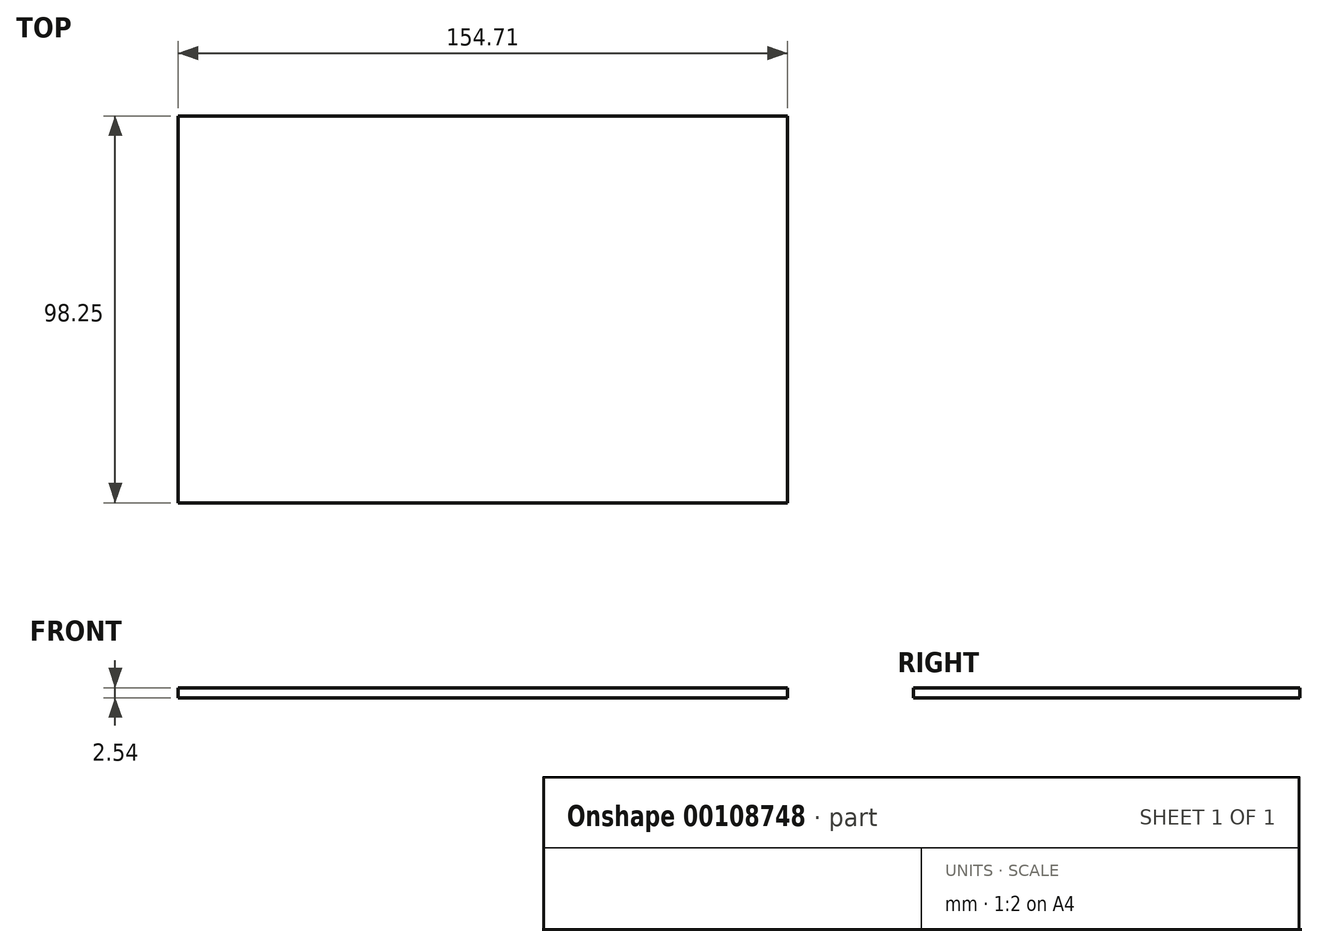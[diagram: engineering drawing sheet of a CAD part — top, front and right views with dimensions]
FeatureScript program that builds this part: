
annotation { "Feature Type Name" : "Feature", "Feature Type Description" : "" }
export const myFeature = defineFeature(function(context is Context, id is Id, definition is map)
    precondition{}
    {
        {
            var Q0;
            Q0=qCreatedBy(makeId("Top.planeOp"),FACE);
            var sketch = newSketch(context, id + "F0", { "sketchPlane" : qUnion([Q0])});
            skLineSegment(sketch, "E0.bottom", {"start": v(-39.4, 27.04) * mm, "end": v(115.3, 27.04) * mm});
            skLineSegment(sketch, "E0.top", {"start": v(-39.4, -71.21) * mm, "end": v(115.3, -71.21) * mm});
            skLineSegment(sketch, "E0.left", {"start": v(-39.4, 27.04) * mm, "end": v(-39.4, -71.21) * mm});
            skLineSegment(sketch, "E0.right", {"start": v(115.3, 27.04) * mm, "end": v(115.3, -71.21) * mm});
            skSolve(sketch);
        }
        {
            var Q0;
            Q0 = qSketchRegion(id + "F0", true);
            extrude(context, id + "F1", {"entities" : qUnion([Q0]), "depth" : 2.54 * mm});
        }
    });
